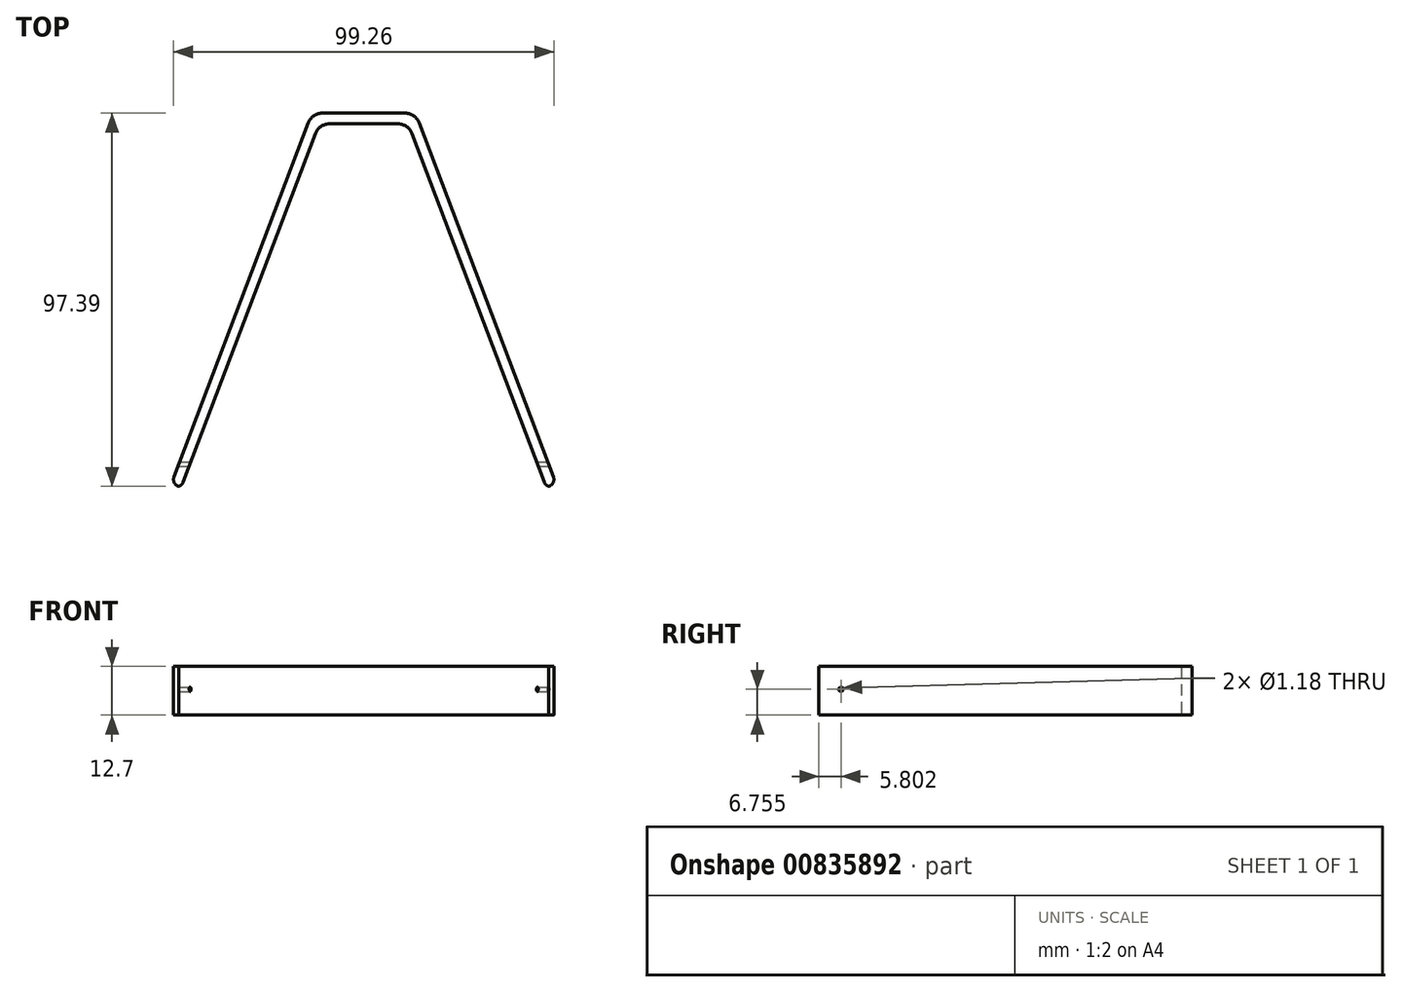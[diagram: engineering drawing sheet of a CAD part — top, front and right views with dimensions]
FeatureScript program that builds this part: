
annotation { "Feature Type Name" : "Feature", "Feature Type Description" : "" }
export const myFeature = defineFeature(function(context is Context, id is Id, definition is map)
    precondition{}
    {
        {
            var Q0;
            Q0=qCreatedBy(makeId("Top.planeOp"),FACE);
            var sketch = newSketch(context, id + "F0", { "sketchPlane" : qUnion([Q0])});
            skLineSegment(sketch, "E0", {"start": v(0, 66.84) * mm, "end": v(-13.52, 66.84) * mm});
            skLineSegment(sketch, "E1", {"start": v(-13.52, 66.84) * mm, "end": v(-50.48, -30.64) * mm});
            skLineSegment(sketch, "E2", {"start": v(-50.48, -30.64) * mm, "end": v(-47.55, -30.64) * mm});
            skLineSegment(sketch, "E3", {"start": v(-47.55, -30.64) * mm, "end": v(-11.65, 64.05) * mm});
            skLineSegment(sketch, "E4", {"start": v(-11.65, 64.05) * mm, "end": v(0, 64.05) * mm});
            skLineSegment(sketch, "E5.MirrorCS", {"start": v(0, 66.84) * mm, "end": v(13.52, 66.84) * mm});
            skLineSegment(sketch, "E6.MirrorCS", {"start": v(11.65, 64.05) * mm, "end": v(0, 64.05) * mm});
            skLineSegment(sketch, "E7.MirrorCS", {"start": v(13.52, 66.84) * mm, "end": v(50.48, -30.64) * mm});
            skLineSegment(sketch, "E8.MirrorCS", {"start": v(47.55, -30.64) * mm, "end": v(11.65, 64.05) * mm});
            skLineSegment(sketch, "E9.MirrorCS", {"start": v(50.48, -30.64) * mm, "end": v(47.55, -30.64) * mm});
            skSolve(sketch);
        }
        {
            var Q0;
            Q0=makeQuery(id+"F0.imprint","IMPRINT",FACE,{"disambiguationData":[TD([[makeQuery(id+"F0.imprint","IMPRINT",EDGE,{"derivedFrom":sQuery(id+"F0.wireOp",EDGE,"E0")}),1.0]])]});
            extrude(context, id + "F1", {"entities" : qUnion([Q0]), "depth" : 12.7 * mm, "offsetDistance" : 25.4 * mm});
        }
        {
            var Q0;
            Q0=makeQuery(id+"F1.opExtrude","SWEPT_EDGE",EDGE,{"disambiguationData":[OSD([sQuery(id+"F0.wireOp",EDGE,"E2"),sQuery(id+"F0.wireOp",EDGE,"E3")])]});
            var Q1;
            Q1=makeQuery(id+"F1.opExtrude","SWEPT_EDGE",EDGE,{"disambiguationData":[OSD([sQuery(id+"F0.wireOp",EDGE,"E1"),sQuery(id+"F0.wireOp",EDGE,"E2")])]});
            var Q2;
            Q2=makeQuery(id+"F1.opExtrude","SWEPT_EDGE",EDGE,{"disambiguationData":[OSD([sQuery(id+"F0.wireOp",EDGE,"E7.MirrorCS"),sQuery(id+"F0.wireOp",EDGE,"E9.MirrorCS")])]});
            var Q3;
            Q3=makeQuery(id+"F1.opExtrude","SWEPT_EDGE",EDGE,{"disambiguationData":[OSD([sQuery(id+"F0.wireOp",EDGE,"E8.MirrorCS"),sQuery(id+"F0.wireOp",EDGE,"E9.MirrorCS")])]});
            fillet(context, id + "F2", {"entities" : qUnion([Q0, Q1, Q2, Q3]), "radius" : 1.9 * mm, "tangentPropagation" : true, "allowEdgeOverflow" : false});
        }
        {
            var Q0;
            Q0=makeQuery(id+"F1.opExtrude","SWEPT_EDGE",EDGE,{"disambiguationData":[OSD([sQuery(id+"F0.wireOp",EDGE,"E5.MirrorCS"),sQuery(id+"F0.wireOp",EDGE,"E7.MirrorCS")])]});
            var Q1;
            Q1=makeQuery(id+"F1.opExtrude","SWEPT_EDGE",EDGE,{"disambiguationData":[OSD([sQuery(id+"F0.wireOp",EDGE,"E0"),sQuery(id+"F0.wireOp",EDGE,"E1")])]});
            var Q2;
            Q2=makeQuery(id+"F1.opExtrude","SWEPT_EDGE",EDGE,{"disambiguationData":[OSD([sQuery(id+"F0.wireOp",EDGE,"E3"),sQuery(id+"F0.wireOp",EDGE,"E4")])]});
            var Q3;
            Q3=makeQuery(id+"F1.opExtrude","SWEPT_EDGE",EDGE,{"disambiguationData":[OSD([sQuery(id+"F0.wireOp",EDGE,"E6.MirrorCS"),sQuery(id+"F0.wireOp",EDGE,"E8.MirrorCS")])]});
            fillet(context, id + "F3", {"entities" : qUnion([Q0, Q1, Q2, Q3]), "radius" : 3.8 * mm, "tangentPropagation" : true, "allowEdgeOverflow" : false});
        }
        {
            var Q0;
            Q0=qCreatedBy(makeId("Right.planeOp"),FACE);
            var sketch = newSketch(context, id + "F4", { "sketchPlane" : qUnion([Q0])});
            skCircle(sketch, "E10", {"center": v(-24.75, 6.75) * mm, "radius": 0.6 * mm});
            skSolve(sketch);
        }
        {
            var Q0;
            Q0=makeQuery(id+"F4.imprint","IMPRINT",FACE,{"disambiguationData":[TD([[makeQuery(id+"F4.imprint","IMPRINT",EDGE,{"derivedFrom":sQuery(id+"F4.wireOp",EDGE,"E10")}),1.0]])]});
            extrude(context, id + "F5", {"entities" : qUnion([Q0]), "operationType" : NewBodyOperationType.REMOVE, "oppositeDirection" : true, "depth" : 57.15 * mm, "offsetDistance" : 25.4 * mm, "hasSecondDirection" : true, "secondDirectionOppositeDirection" : false, "secondDirectionDepth" : 73.9 * mm});
        }
    });
